# Revit family: Mirror-IlluminatedMirror-Vitra-DeluxeSeries-62575+62576+62577
name_source: partatom
category: Furniture Systems
revit_build: Autodesk Revit 2017 (Build: 20160225_1515(x64)
units: mm (PartAtom-declared; Revit-internal decimal feet)

## family parameters
Cut with Voids When Loaded = No
Host = Face
OmniClass Number = 23.40.00.00
OmniClass Title = Equipment and Furnishings
Part Type = Normal
Room Calculation Point = No
Round Connector Dimension = Use Diameter
Shared = Yes

## types (3) — shared parameters
BIMobject category = Sanitary - Mirrors
Brand = VitrA
Construction Type = Wall Mounted
Depth(mm) = 45 mm
Design country = Turkey
IFC Classification = Furnishing Element
Lighting Type = Ambiance Led Lighting
Manufacturer = Vitra
Manufacturer name = Vitra
Masterformat 2014 Code = 12 50 00
Masterformat 2014 Description = Furniture
NBS Referans Code = 45-55-06
NBS Referans Description = Bathroom Mirrors
Nominal height = 0.000
Nominal width = 0.000
OmniClass Code = 23-21 37 13 15
OmniClass Description = Mirrors
Primary Material = Vitra-Mirror
Product certification = https://vitraglobal.com
Product family = Deluxe
Product group = Bathroom Furniture
Secondary Material = Vitra-MattGrey
Technical description = https://www.vitra.com.tr
Third Material = Vitra-Light
UNSPSC Code = 56
UNSPSC Description = Furniture and Furnishings
URL = https://vitraglobal.com
Uniclass 1.4 Code = L8732
Uniclass 1.4 Description = Mirrors
Uniclass 2.0 Code = PR-45-55-06
Uniclass 2.0 Description = Bathroom Mirrors
Uniclass 2015 Code = Pr_25_71_53_06
Uniclass 2015 Name = Bathroom mirrors
Uniformat II Code = E2010
Uniformat II Description = Furnishings
Voltage = 220V
Warranty Period (Year) = 2
Youtube = https://www.youtube.com
zero-valued in all types: Default Elevation

## per-type parameters (varying)
| type | Article No. (default) | Description | Diameter | Height(mm) | Model | Product SKU | Product data url | Product url | Weight Net (kg) | Width(mm) |
| Mirror(IlluminatedMirror)(BackLighting)-Vitra-DeluxeSeries(60cm)_62575 | 62575 | Deluxe Illuminated Mirror 60 cm | 304 mm  [stored 0.997375 ft] | 600 mm | 62575 | 62575 |  | https://www.vitraglobal.com | 10,600 | 600 mm |
| Mirror(IlluminatedMirror)(BackLighting)-Vitra-DeluxeSeries(80cm)_62576 | 62576 | Deluxe Illuminated Mirror 80 cm | 404 mm  [stored 1.32546 ft] | 800 mm  [stored 2.62467 ft] | 62576 | 62576 | https://www.vitra.com.tr |  | 12,100 | 800 mm  [stored 2.62467 ft] |
| Mirror(IlluminatedMirror)(BackLighting)-Vitra-DeluxeSeries(110cm)_62577 | 62577 | Deluxe Illuminated Mirror 110 cm | 554 mm  [stored 1.81759 ft] | 1100 mm | 62577 | 62577 |  | https://www.vitra.com.tr | 27,000 | 1100 mm |

note: [stored X ft] marks values corroborated as IEEE doubles in the binary element streams (Revit-internal decimal feet)

## geometry (parser evidence)
native form markers: Sweep x2
no freeform markers — native parametric forms only
